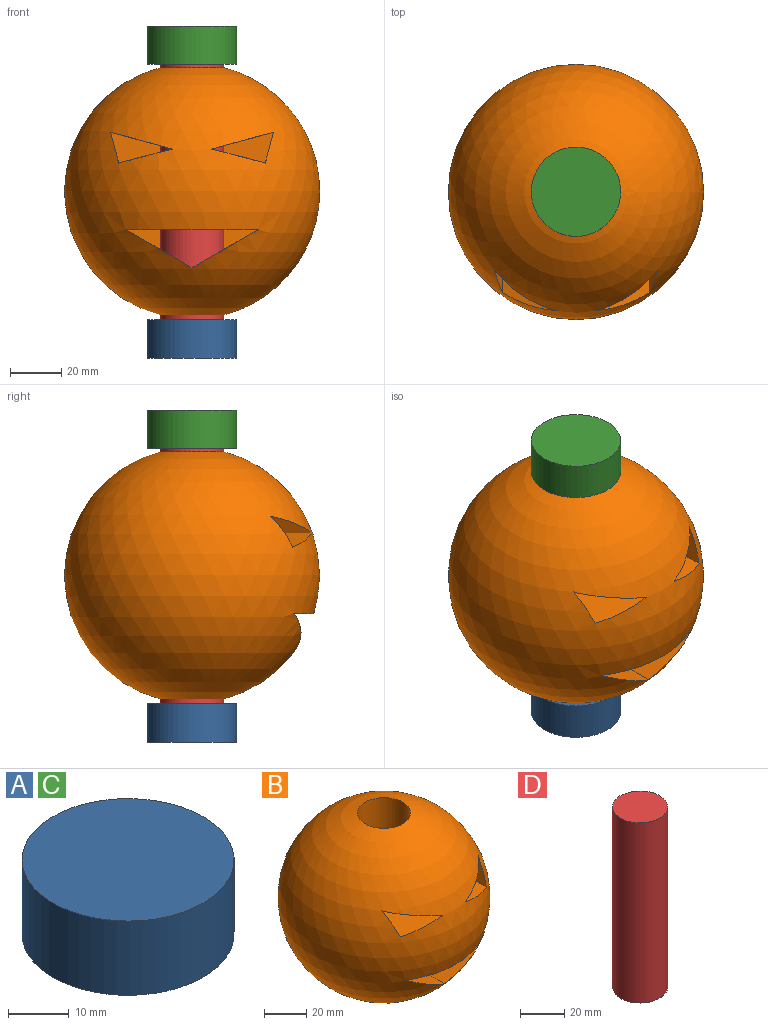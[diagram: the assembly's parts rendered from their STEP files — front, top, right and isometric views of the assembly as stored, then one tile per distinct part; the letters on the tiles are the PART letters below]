
ASSEMBLY  parts=4 mates=4
PART A: 3 faces, bbox 35x35x15 mm
  f0: cylinder r=17.5mm len=35mm, axis (0,0,-1), area 1649.3mm2, adj f1,f2
  f1: plane 35x35mm, normal (0,0,1), area 962.1mm2, adj f0
  f2: plane 35x35mm, normal (0,0,-1), area 962.1mm2, adj f0
PART B: 15 faces, bbox 100x100x96.8 mm
  f0: sphere r=50mm, area 29643.5mm2, adj f1,f2,f3,f4,f6,f7,f8,f10
  f1: cylinder r=12.5mm len=96.82mm, axis (0,0,-1), area 7158.2mm2, adj f0,f3,f4,f5,f7,f8,f9,f10
  f2: plane 39.43x12.09mm, normal (0.97,0,0.25), area 445.7mm2, adj f0,f3,f4,f5
  f3: plane 46.54x24.11mm, normal (-0.26,0,-0.96), area 979.1mm2, adj f0,f1,f2,f4,f5
  f4: plane 46.54x20.94mm, normal (-0.25,0,0.97), area 918.6mm2, adj f0,f1,f2,f3,f5
  f5: plane 19.37x12.09mm, normal (0,-1,0), area 129.3mm2, adj f1,f2,f3,f4
  f6: plane 39.43x12.09mm, normal (-0.97,0,0.25), area 445.7mm2, adj f0,f7,f8,f9
  f7: plane 46.54x20.94mm, normal (0.25,0,0.97), area 918.6mm2, adj f0,f1,f6,f8,f9
  f8: plane 46.54x24.11mm, normal (0.26,0,-0.96), area 979.1mm2, adj f0,f1,f6,f7,f9
  f9: plane 19.37x12.09mm, normal (0,-1,0), area 129.3mm2, adj f1,f6,f7,f8
  f10: plane 51.96x47.7mm, normal (0,0,-1), area 2104.3mm2, adj f0,f1,f11,f12,f13,f14
  f11: plane 42.72x25.98mm, normal (0.5,0,0.87), area 1113.1mm2, adj f0,f1,f10,f12,f13
  f12: plane 42.72x25.98mm, normal (-0.5,0,0.87), area 1113.1mm2, adj f0,f1,f10,f11,f14
  f13: plane 13.48x7.78mm, normal (0,-1,0), area 52.5mm2, adj f1,f10,f11
  f14: plane 13.48x7.78mm, normal (0,-1,0), area 52.5mm2, adj f1,f10,f12
PART C: same geometry as A
PART D: 3 faces, bbox 25x25x100 mm
  f0: cylinder r=12.5mm len=100mm, axis (0,0,-1), area 7854mm2, adj f1,f2
  f1: plane 25x25mm, normal (0,0,1), area 490.9mm2, adj f0
  f2: plane 25x25mm, normal (0,0,-1), area 490.9mm2, adj f0
PLACE A t=(83.88,130.97,-27.37)mm
PLACE B t=(83.88,130.97,37.91)mm
PLACE C t=(83.88,130.97,87.63)mm
PLACE D t=(83.88,130.97,-12.37)mm
MATE fastened B.f1 <-> B.f1  axis (0,0,1) through (83.88,130.97,37.91)mm
MATE slider B.f1 <-> D.f0  axis (0,0,-1) through (83.88,130.97,86.32)mm
MATE fastened A.f0 <-> D.f0  axis (0,0,1) through (83.88,130.97,-12.37)mm
MATE fastened C.f0 <-> D.f0  axis (0,0,-1) through (83.88,130.97,87.63)mm
